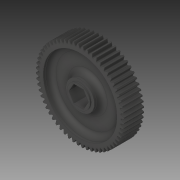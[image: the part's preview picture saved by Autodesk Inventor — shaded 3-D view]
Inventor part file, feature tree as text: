
AUTODESK INVENTOR PART (.ipt)
format: ipt  version: 2019 (Build 230136000, 136)  size: 653,312 bytes
history: native  units: in
note: dims shown in document units (in); Inventor stores cm internally (conversion verified against a paired STEP export)
features: mirror x1
ambient origin geometry x8: Origin, YZ Plane, XZ Plane, XY Plane, X Axis, Y Axis, Z Axis, Center Point
bodies: Solid1 (feature_tree)
feature tree (1):
  mirror  "Mirror1"
